# Revit family: for update_74806XXX_new
name_source: partatom
category: Plumbing Fixtures
revit_build: Autodesk Revit 2018 (Build: 20170223_1515(x64)
units: mm (PartAtom-declared; Revit-internal decimal feet)

## family parameters
Cut with Voids When Loaded = Yes
Host = Face
OmniClass Number = 23.31.11.00
OmniClass Title = Faucets
Part Type = Normal
Room Calculation Point = No
Round Connector Dimension = Use Diameter
Shared = No

## types (3) — shared parameters
Always visible = Yes
BIMobject category = Taps & Mixers
Connector Description = Water Outlet 9.5 mm
Date Updated = 2023/08/04
Date of publishing = 02.11.2022 0:00:00
Default Elevation = 1219 mm
Description = Zesis M33 Single lever kitchen mixer 150, LowPressure/vented hot water cylinders, 1jet
Design country = Germany
Diameter = 10 mm  [stored 0.0328084 ft]
EAN code = 4059625340202
Edition number = 1
IFC Classification = Valve
Inlet Connector Description = Water Inlet 9.5 mm
Inlet Diameter = 10 mm  [stored 0.0328084 ft]
Manufacturer = Hansgrohe
Manufacturer country = Germany
Manufacturer name = hansgrohe
Masterformat 2014 Code = 22 41 23
Masterformat 2014 Description = Residential Showers
Model = 74806XXX
OmniClass Code = 23-31 11 00
OmniClass Description = Faucets
Product Guid = ead4b97e-c28f-40a0-b2bc-0f687ebaf8f5
Product SKU = 74806XXX
Product data url = https://bimobject.com
Product family = Kitchen mixers
Product group = Zesis M33
Product name = Zesis M33 Single lever kitchen mixer 150, LowPressure/vented hot water cylinders, 1jet
Product url = https://pro.hansgrohe.com
QR code = https://bimobject.com
UNSPSC Code = 30181503
URL = https://www.hansgrohe.com
Uniclass 2015 Code = Pr_40_20_87_76
Uniclass 2015 Name = Shower heads
Uniformat II Code = D2010
Uniformat II Description = Plumbing Fixtures
Version = 1
Weight Net (Kg) = 1,6

## per-type parameters (varying)
| type | Material |
| 670 Matte Black | Hansgrohe - Metal - 670 Matte Black |
| 000 Chrome | Hansgrohe - Metal - 000 Chrome |
| 800 Stainless Steel Optic | Hansgrohe - Metal - 800 Stainless Steel Optic |

note: [stored X ft] marks values corroborated as IEEE doubles in the binary element streams (Revit-internal decimal feet)

## geometry (parser evidence)
native form markers: Sweep x1
no freeform markers — native parametric forms only
